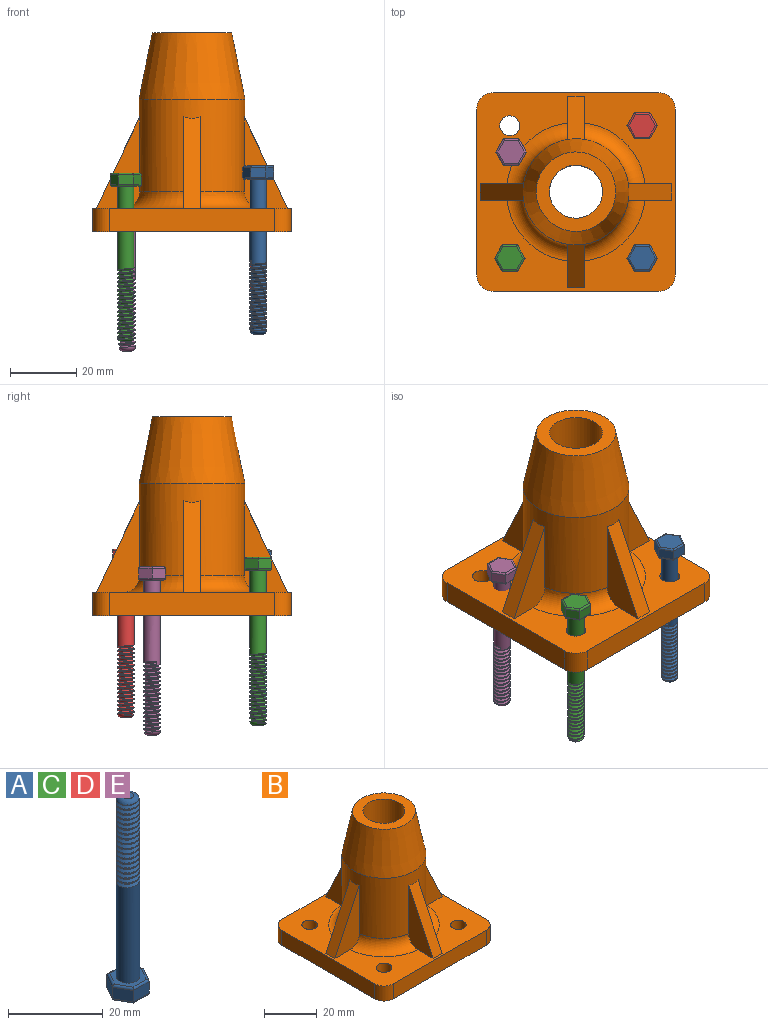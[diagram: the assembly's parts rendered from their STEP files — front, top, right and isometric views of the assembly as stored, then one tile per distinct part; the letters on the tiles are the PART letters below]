
ASSEMBLY  parts=5 mates=3
PART A: 44 faces, bbox 9.2x8x50.8 mm
  f0: torus R=1.23mm, axis (0,0,1), area 20.2mm2, adj f1,f18,f29,f30,f31
  f1: cylinder r=2.5mm len=2.39mm, axis (0,0,-1), area 0.4mm2, adj f0,f2,f29
  f2: cylinder r=2.5mm len=5mm, axis (0,0,-1), area 4mm2, adj f1,f3,f29,f30
  f3: cylinder r=2.5mm len=5mm, axis (0,0,-1), area 4mm2, adj f2,f4,f29,f30
  f4: cylinder r=2.5mm len=5mm, axis (0,0,-1), area 4mm2, adj f3,f5,f29,f30
  f5: cylinder r=2.5mm len=5mm, axis (0,0,-1), area 4mm2, adj f4,f6,f29,f30
  f6: cylinder r=2.5mm len=5mm, axis (0,0,-1), area 4mm2, adj f5,f7,f29,f30
  f7: cylinder r=2.5mm len=5mm, axis (0,0,-1), area 4mm2, adj f6,f8,f29,f30
  f8: cylinder r=2.5mm len=5mm, axis (0,0,-1), area 4mm2, adj f7,f9,f29,f30
  f9: cylinder r=2.5mm len=5mm, axis (0,0,-1), area 4mm2, adj f8,f10,f29,f30
  f10: cylinder r=2.5mm len=5mm, axis (0,0,-1), area 4mm2, adj f9,f11,f29,f30
  f11: cylinder r=2.5mm len=5mm, axis (0,0,-1), area 4mm2, adj f10,f12,f29,f30
  f12: cylinder r=2.5mm len=5mm, axis (0,0,-1), area 4mm2, adj f11,f13,f29,f30
  f13: cylinder r=2.5mm len=5mm, axis (0,0,-1), area 4mm2, adj f12,f14,f29,f30
  f14: cylinder r=2.5mm len=5mm, axis (0,0,-1), area 4mm2, adj f13,f15,f29,f30
  f15: cylinder r=2.5mm len=5mm, axis (0,0,-1), area 4mm2, adj f14,f16,f29,f30
  f16: cylinder r=2.5mm len=5mm, axis (0,0,-1), area 4mm2, adj f15,f17,f29,f30
  f17: cylinder r=2.5mm len=26.48mm, axis (0,0,-1), area 396.4mm2, adj f16,f25,f28,f29,f30
  f18: plane 2.46x2.46mm, normal (0,0,1), area 4.8mm2, adj f0
  f19: plane 4x2.98mm, normal (0.87,-0.5,0), area 13.8mm2, adj f20,f24,f33,f39
  f20: plane 4x2.98mm, normal (0.87,0.5,0), area 13.8mm2, adj f19,f21,f32,f38
  f21: plane 4.62x2.98mm, normal (0,1,0), area 13.8mm2, adj f20,f22,f34,f40
  f22: plane 4x2.98mm, normal (-0.87,0.5,0), area 13.8mm2, adj f21,f23,f36,f42
  f23: plane 4x2.98mm, normal (-0.87,-0.5,0), area 13.8mm2, adj f22,f24,f37,f43
  f24: plane 4.62x2.98mm, normal (0,-1,0), area 13.8mm2, adj f19,f23,f35,f41
  f25: plane 8.06x6.98mm, normal (0,0,1), area 22.6mm2, adj f17,f38,f39,f40,f41,f42,f43
  f26: plane 8.06x6.98mm, normal (0,0,-1), area 42.2mm2, adj f32,f33,f34,f35,f36,f37
  f27: plane 0.06x0.05mm, normal (0,-1,0), area 0mm2, adj f29,f30,f31
  f28: plane 1.02x0.41mm, normal (-0.59,-0.81,0), area 0.3mm2, adj f17,f29,f30
  f29: bspline ~21.86x5.77mm, area 167.5mm2, adj f0,f1,f2,f3,f4,f5,f6,f7
  f30: bspline ~21.86x5.77mm, area 168.7mm2, adj f0,f2,f3,f4,f5,f6,f7,f8
  f31: bspline ~0.94x0.6mm, area 0.3mm2, adj f0,f27,f29,f30
  f32: cylinder r=0.51mm len=4.25mm, axis (-0.5,0.87,0), area 3.5mm2, adj f20,f26,f33,f34
  f33: cylinder r=0.51mm len=4.25mm, axis (0.5,0.87,0), area 3.5mm2, adj f19,f26,f32,f35
  f34: cylinder r=0.51mm len=4.62mm, axis (-1,0,0), area 3.5mm2, adj f21,f26,f32,f36
  f35: cylinder r=0.51mm len=4.62mm, axis (1,0,0), area 3.5mm2, adj f24,f26,f33,f37
  f36: cylinder r=0.51mm len=4.25mm, axis (-0.5,-0.87,0), area 3.5mm2, adj f22,f26,f34,f37
  f37: cylinder r=0.51mm len=4.25mm, axis (0.5,-0.87,0), area 3.5mm2, adj f23,f26,f35,f36
  f38: cylinder r=0.51mm len=4.25mm, axis (0.5,-0.87,0), area 3.5mm2, adj f20,f25,f39,f40
  f39: cylinder r=0.51mm len=4.25mm, axis (-0.5,-0.87,0), area 3.5mm2, adj f19,f25,f38,f41
  f40: cylinder r=0.51mm len=4.62mm, axis (1,0,0), area 3.5mm2, adj f21,f25,f38,f42
  f41: cylinder r=0.51mm len=4.62mm, axis (-1,0,0), area 3.5mm2, adj f24,f25,f39,f43
  f42: cylinder r=0.51mm len=4.25mm, axis (0.5,0.87,0), area 3.5mm2, adj f22,f25,f40,f43
  f43: cylinder r=0.51mm len=4.25mm, axis (-0.5,0.87,0), area 3.5mm2, adj f23,f25,f41,f42
PART B: 34 faces, bbox 60x60x60 mm
  f0: cylinder r=16mm len=32mm, axis (0,0,-1), area 2365.7mm2, adj f1,f2,f3,f20,f21,f22,f23,f24
  f1: torus R=21mm, axis (0,0,1), area 180.4mm2, adj f0,f15,f27,f30
  f2: torus R=21mm, axis (0,0,1), area 180.4mm2, adj f0,f15,f26,f32
  f3: torus R=21mm, axis (0,0,1), area 180.4mm2, adj f0,f15,f23,f33
  f4: cylinder r=8mm len=60mm, axis (0,0,-1), area 3015.9mm2, adj f5,f6
  f5: plane 24x24mm, normal (0,0,1), area 251.3mm2, adj f4,f21
  f6: plane 60x60mm, normal (0,0,-1), area 3264.4mm2, adj f4,f7,f8,f9,f10,f11,f12,f13
  f7: plane 50x7mm, normal (1,0,0), area 350mm2, adj f6,f15,f16,f19
  f8: plane 50x7mm, normal (0,1,0), area 350mm2, adj f6,f15,f16,f17
  f9: plane 50x7mm, normal (-1,0,0), area 350mm2, adj f6,f15,f17,f18
  f10: cylinder r=3mm len=7mm, axis (0,0,-1), area 131.9mm2, adj f6,f15
  f11: cylinder r=3mm len=7mm, axis (0,0,-1), area 131.9mm2, adj f6,f15
  f12: cylinder r=3mm len=7mm, axis (0,0,-1), area 131.9mm2, adj f6,f15
  f13: plane 50x7mm, normal (0,-1,0), area 350mm2, adj f6,f15,f18,f19
  f14: cylinder r=3mm len=7mm, axis (0,0,-1), area 131.9mm2, adj f6,f15
  f15: plane 60x60mm, normal (0,0,1), area 1921.4mm2, adj f1,f2,f3,f7,f8,f9,f10,f11
  f16: cylinder r=5mm len=7mm, axis (0,0,1), area 55mm2, adj f6,f7,f8,f15
  f17: cylinder r=5mm len=7mm, axis (0,0,-1), area 55mm2, adj f6,f8,f9,f15
  f18: cylinder r=5mm len=7mm, axis (0,0,1), area 55mm2, adj f6,f9,f13,f15
  f19: cylinder r=5mm len=7mm, axis (0,0,-1), area 55mm2, adj f6,f7,f13,f15
  f20: torus R=21mm, axis (0,0,1), area 180.4mm2, adj f0,f15,f24,f29
  f21: cone r=12mm half-angle=11.3deg, axis (0,0,-1), area 1794.1mm2, adj f0,f5
  f22: plane 27.64x13.07mm, normal (0,-0.9,0.43), area 151.4mm2, adj f0,f15,f23,f24
  f23: plane 27.65x13.08mm, normal (1,0,0), area 175.3mm2, adj f0,f3,f15,f22
  f24: plane 27.65x13.08mm, normal (-1,0,0), area 175.3mm2, adj f0,f15,f20,f22
  f25: plane 27.64x13.07mm, normal (0,0.9,0.43), area 151.4mm2, adj f0,f15,f26,f27
  f26: plane 27.65x13.08mm, normal (1,0,0), area 175.3mm2, adj f0,f2,f15,f25
  f27: plane 27.65x13.08mm, normal (-1,0,0), area 175.3mm2, adj f0,f1,f15,f25
  f28: plane 27.64x13.07mm, normal (-0.9,0,0.43), area 151.4mm2, adj f0,f15,f29,f30
  f29: plane 27.65x13.08mm, normal (0,-1,0), area 175.3mm2, adj f0,f15,f20,f28
  f30: plane 27.65x13.08mm, normal (0,1,0), area 175.3mm2, adj f0,f1,f15,f28
  f31: plane 27.64x13.07mm, normal (0.9,0,0.43), area 151.4mm2, adj f0,f15,f32,f33
  f32: plane 27.65x13.08mm, normal (0,1,0), area 175.3mm2, adj f0,f2,f15,f31
  f33: plane 27.65x13.08mm, normal (0,-1,0), area 175.3mm2, adj f0,f3,f15,f31
PART C: same geometry as A
PART D: same geometry as A
PART E: same geometry as A
PLACE A rot(axis=(1,0,0),180deg) t=(21.22,-20.54,10.41)mm
PLACE B rot(axis=(1,0,0),0deg) t=(1.22,-0.54,-9.42)mm
PLACE C rot(axis=(0,-1,0),180deg) t=(-18.78,-20.54,8.23)mm
PLACE D rot(axis=(0,-1,0),180deg) t=(21.22,19.46,10.68)mm
PLACE E rot(axis=(1,0,0),180deg) t=(-18.36,11.51,5.33)mm
MATE slider C.f0 <-> B.f10  axis (0,0,1) through (-18.78,-20.54,-18.54)mm
MATE slider D.f0 <-> B.f12  axis (0,0,1) through (21.22,19.46,-16.08)mm
MATE slider A.f0 <-> B.f11  axis (0,0,1) through (21.22,-20.54,-16.35)mm
